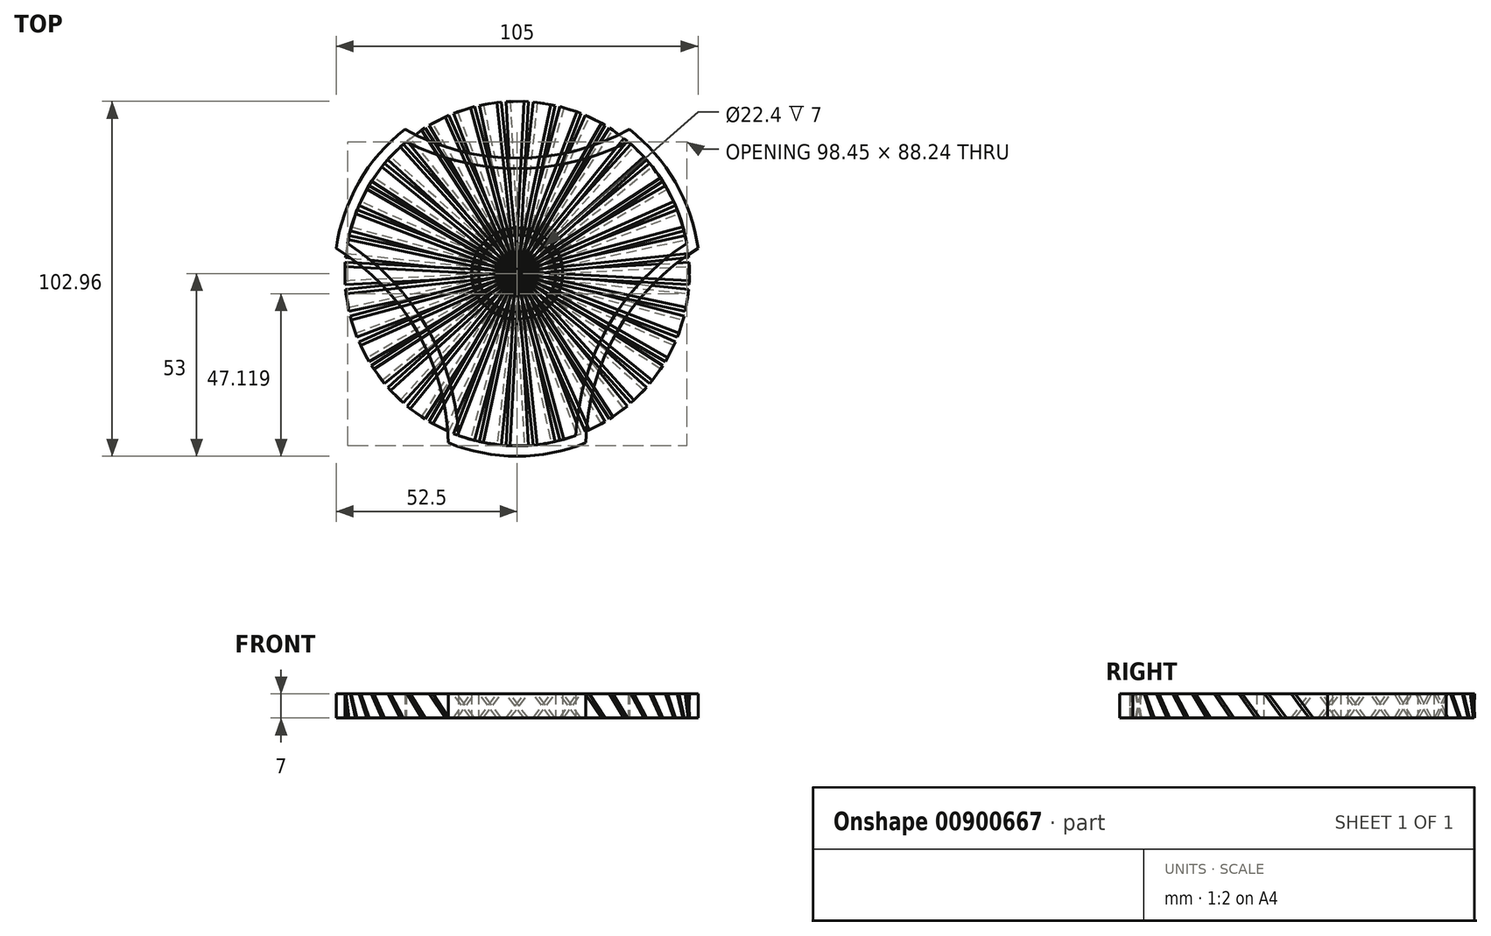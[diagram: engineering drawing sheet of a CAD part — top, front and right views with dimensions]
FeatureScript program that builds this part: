
annotation { "Feature Type Name" : "Feature", "Feature Type Description" : "" }
export const myFeature = defineFeature(function(context is Context, id is Id, definition is map)
    precondition{}
    {
        {
            var Q0;
            Q0=qCreatedBy(makeId("Top.planeOp"),FACE);
            var sketch = newSketch(context, id + "F0", { "sketchPlane" : qUnion([Q0])});
            skLineSegment(sketch, "E0.bottom", {"start": v(-3.22, 49.9) * mm, "end": v(-2.02, 49.96) * mm});
            skLineSegment(sketch, "E0.top", {"start": v(2.02, -49.96) * mm, "end": v(3.22, -49.9) * mm});
            skLineSegment(sketch, "E0.left", {"start": v(-3.22, 49.9) * mm, "end": v(2.02, -49.96) * mm});
            skLineSegment(sketch, "E0.right", {"start": v(-2.02, 49.96) * mm, "end": v(3.22, -49.9) * mm});
            skPoint(sketch, "E0.middle", {"position": v(0, 0) * mm});
            skSolve(sketch);
        }
        {
            var Q0;
            Q0=qCreatedBy(makeId("Top.planeOp"),FACE);
            cPlane(context, id + "F1", {"entities" : qUnion([Q0]), "cplaneType" : CPlaneType.OFFSET, "offset" : 7 * mm, "width" : 150 * mm, "height" : 150 * mm});
        }
        {
            var Q0;
            Q0=qCreatedBy(id+"F1.planeOp",FACE);
            var sketch = newSketch(context, id + "F2", { "sketchPlane" : qUnion([Q0])});
            skLineSegment(sketch, "E1.bottom", {"start": v(2.02, 49.96) * mm, "end": v(3.22, 49.9) * mm});
            skLineSegment(sketch, "E1.top", {"start": v(-3.22, -49.9) * mm, "end": v(-2.02, -49.96) * mm});
            skLineSegment(sketch, "E1.left", {"start": v(2.02, 49.96) * mm, "end": v(-3.22, -49.9) * mm});
            skLineSegment(sketch, "E1.right", {"start": v(3.22, 49.9) * mm, "end": v(-2.02, -49.96) * mm});
            skPoint(sketch, "E1.middle", {"position": v(0, 0) * mm});
            skSolve(sketch);
        }
        {
            var Q0;
            Q0=makeQuery(id+"F0.imprint","IMPRINT",FACE,{"disambiguationData":[TD([[makeQuery(id+"F0.imprint","IMPRINT",EDGE,{"derivedFrom":sQuery(id+"F0.wireOp",EDGE,"E0.bottom")}),-1.0]])]});
            var Q1;
            Q1=makeQuery(id+"F2.imprint","IMPRINT",FACE,{"disambiguationData":[TD([[makeQuery(id+"F2.imprint","IMPRINT",EDGE,{"derivedFrom":sQuery(id+"F2.wireOp",EDGE,"E1.bottom")}),-1.0]])]});
            loft(context, id + "F3", {"sheetProfilesArray" : [{ "sheetProfileEntities" : qUnion([Q0]) }, { "sheetProfileEntities" : qUnion([Q1]) }]});
        }
        {
            var Q0;
            Q0=qCreatedBy(makeId("Right.planeOp"),FACE);
            var sketch = newSketch(context, id + "F4", { "sketchPlane" : qUnion([Q0])});
            skLineSegment(sketch, "E2", {"start": v(0, 0) * mm, "end": v(0, 29.85) * mm});
            skSolve(sketch);
        }
        {
            var Q0;
            Q0=makeQuery(id+"F3.opLoft","SWEPT_BODY",BODY,{"disambiguationData":[OSD([makeQuery(id+"F0.imprint","IMPRINT",FACE,{"disambiguationData":[TD([[makeQuery(id+"F0.imprint","IMPRINT",EDGE,{"derivedFrom":sQuery(id+"F0.wireOp",EDGE,"E0.bottom")}),-1.0]])]}),makeQuery(id+"F2.imprint","IMPRINT",FACE,{"disambiguationData":[TD([[makeQuery(id+"F2.imprint","IMPRINT",EDGE,{"derivedFrom":sQuery(id+"F2.wireOp",EDGE,"E1.bottom")}),-1.0]])]})])]});
            var Q1;
            Q1=sQuery(id+"F4.wireOp",EDGE,"E2");
            circularPattern(context, id + "F5", {"entities" : qUnion([Q0]), "axis" : qUnion([Q1]), "angle" : 360 * degree, "instanceCount" : 40, "equalSpace" : true});
        }
        {
            var Q0;
            Q0=qCreatedBy(makeId("Top.planeOp"),FACE);
            var sketch = newSketch(context, id + "F6", { "sketchPlane" : qUnion([Q0])});
            skArc(sketch, "E3", {"start": v(-32.22, 38.24) * mm, "mid": v(-43.3, 25) * mm, "end": v(-49.22, 8.78) * mm});
            skLineSegment(sketch, "E4", {"start": v(-32.22, 38.24) * mm, "end": v(32.22, 38.24) * mm, "construction": true});
            skArc(sketch, "E5", {"start": v(-32.22, 38.24) * mm, "mid": v(0, 30.5) * mm, "end": v(32.22, 38.24) * mm});
            skArc(sketch, "E6.1.0", {"start": v(-17, -47.02) * mm, "mid": v(-26.42, -15.25) * mm, "end": v(-49.22, 8.78) * mm});
            skArc(sketch, "E6.2.0", {"start": v(49.22, 8.78) * mm, "mid": v(26.42, -15.25) * mm, "end": v(17, -47.02) * mm});
            skArc(sketch, "E7.trimOffspring", {"start": v(49.22, 8.78) * mm, "mid": v(43.3, 25) * mm, "end": v(32.22, 38.24) * mm});
            skArc(sketch, "E8.trimOffspring", {"start": v(-17, -47.02) * mm, "mid": v(0, -50) * mm, "end": v(17, -47.02) * mm});
            skArc(sketch, "E9.0", {"start": v(-32.57, 41.81) * mm, "mid": v(0, 33.5) * mm, "end": v(32.57, 41.81) * mm});
            skArc(sketch, "E9.1", {"start": v(-19.93, -49.11) * mm, "mid": v(-29.02, -16.75) * mm, "end": v(-52.5, 7.3) * mm});
            skArc(sketch, "E9.2", {"start": v(-19.93, -49.11) * mm, "mid": v(0, -53) * mm, "end": v(19.93, -49.11) * mm});
            skArc(sketch, "E9.3", {"start": v(-32.57, 41.81) * mm, "mid": v(-45.9, 26.5) * mm, "end": v(-52.5, 7.3) * mm});
            skArc(sketch, "E9.4", {"start": v(52.5, 7.3) * mm, "mid": v(29.02, -16.75) * mm, "end": v(19.93, -49.11) * mm});
            skArc(sketch, "E9.5", {"start": v(52.5, 7.3) * mm, "mid": v(45.9, 26.5) * mm, "end": v(32.57, 41.81) * mm});
            skCircle(sketch, "E10", {"center": v(0, 0) * mm, "radius": 11.2 * mm});
            skCircle(sketch, "E11", {"center": v(0, 0) * mm, "radius": 13.2 * mm});
            skSolve(sketch);
        }
        {
            var Q0;
            Q0=makeQuery(id+"F6.imprint","IMPRINT",FACE,{"disambiguationData":[TD([[makeQuery(id+"F6.imprint","IMPRINT",EDGE,{"derivedFrom":sQuery(id+"F6.wireOp",EDGE,"E3")}),-1.0]])]});
            var Q1;
            Q1=makeQuery(id+"F6.imprint","IMPRINT",FACE,{"disambiguationData":[TD([[makeQuery(id+"F6.imprint","IMPRINT",EDGE,{"derivedFrom":sQuery(id+"F6.wireOp",EDGE,"E10")}),-1.0]])]});
            extrude(context, id + "F7", {"entities" : qUnion([Q0, Q1]), "depth" : 7 * mm, "offsetDistance" : 25 * mm});
        }
    });
